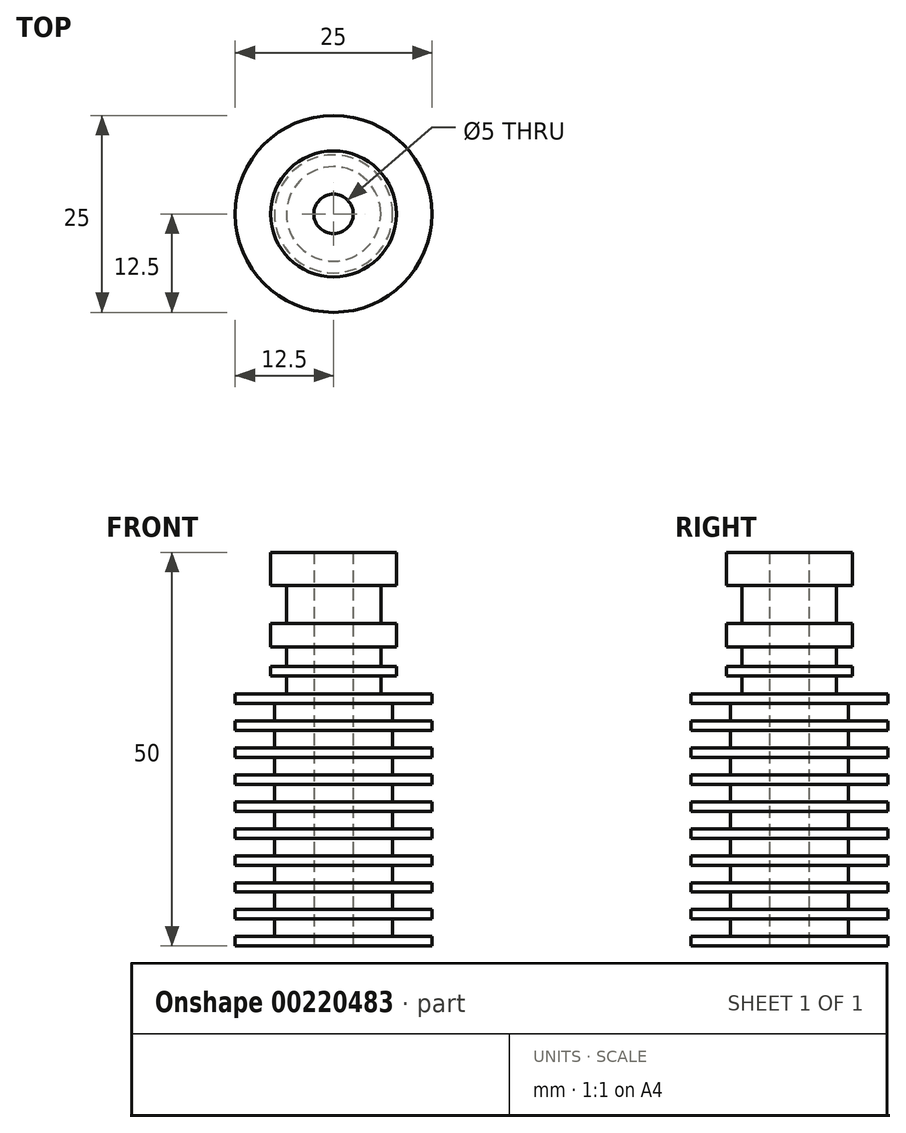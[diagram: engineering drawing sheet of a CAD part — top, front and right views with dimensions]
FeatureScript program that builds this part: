
annotation { "Feature Type Name" : "Feature", "Feature Type Description" : "" }
export const myFeature = defineFeature(function(context is Context, id is Id, definition is map)
    precondition{}
    {
        {
            var Q0;
            Q0=qCreatedBy(makeId("Front.planeOp"),FACE);
            var sketch = newSketch(context, id + "F0", { "sketchPlane" : qUnion([Q0])});
            skLineSegment(sketch, "E0", {"start": v(0, 0) * mm, "end": v(12.5, 0) * mm});
            skLineSegment(sketch, "E1", {"start": v(12.5, 0) * mm, "end": v(12.5, 1.2) * mm});
            skLineSegment(sketch, "E2", {"start": v(12.5, 1.2) * mm, "end": v(7.5, 1.2) * mm});
            skLineSegment(sketch, "E3", {"start": v(7.5, 1.2) * mm, "end": v(7.5, 3.42) * mm});
            skLineSegment(sketch, "E4", {"start": v(7.5, 3.42) * mm, "end": v(12.5, 3.42) * mm});
            skLineSegment(sketch, "E5", {"start": v(12.5, 3.42) * mm, "end": v(12.5, 4.62) * mm});
            skLineSegment(sketch, "E6", {"start": v(12.5, 4.62) * mm, "end": v(7.5, 4.62) * mm});
            skLineSegment(sketch, "E7", {"start": v(7.5, 4.62) * mm, "end": v(7.5, 6.84) * mm});
            skLineSegment(sketch, "E8", {"start": v(7.5, 6.84) * mm, "end": v(12.5, 6.84) * mm});
            skLineSegment(sketch, "E9", {"start": v(12.5, 6.84) * mm, "end": v(12.5, 8.04) * mm});
            skLineSegment(sketch, "E10", {"start": v(12.5, 8.04) * mm, "end": v(7.5, 8.04) * mm});
            skLineSegment(sketch, "E11", {"start": v(7.5, 8.04) * mm, "end": v(7.5, 10.27) * mm});
            skLineSegment(sketch, "E12", {"start": v(7.5, 10.27) * mm, "end": v(12.5, 10.27) * mm});
            skLineSegment(sketch, "E13", {"start": v(12.5, 10.27) * mm, "end": v(12.5, 11.47) * mm});
            skLineSegment(sketch, "E14", {"start": v(12.5, 11.47) * mm, "end": v(7.5, 11.47) * mm});
            skLineSegment(sketch, "E15", {"start": v(7.5, 11.47) * mm, "end": v(7.5, 13.69) * mm});
            skLineSegment(sketch, "E16", {"start": v(7.5, 13.69) * mm, "end": v(12.5, 13.69) * mm});
            skLineSegment(sketch, "E17", {"start": v(12.5, 13.69) * mm, "end": v(12.5, 14.89) * mm});
            skLineSegment(sketch, "E18", {"start": v(12.5, 14.89) * mm, "end": v(7.5, 14.89) * mm});
            skLineSegment(sketch, "E19", {"start": v(7.5, 14.89) * mm, "end": v(7.5, 17.11) * mm});
            skLineSegment(sketch, "E20", {"start": v(7.5, 17.11) * mm, "end": v(12.5, 17.11) * mm});
            skLineSegment(sketch, "E21", {"start": v(12.5, 17.11) * mm, "end": v(12.5, 18.31) * mm});
            skLineSegment(sketch, "E22", {"start": v(12.5, 18.31) * mm, "end": v(7.5, 18.31) * mm});
            skLineSegment(sketch, "E23", {"start": v(7.5, 18.31) * mm, "end": v(7.5, 20.53) * mm});
            skLineSegment(sketch, "E24", {"start": v(7.5, 20.53) * mm, "end": v(12.5, 20.53) * mm});
            skLineSegment(sketch, "E25", {"start": v(12.5, 20.53) * mm, "end": v(12.5, 21.73) * mm});
            skLineSegment(sketch, "E26", {"start": v(12.5, 21.73) * mm, "end": v(7.5, 21.73) * mm});
            skLineSegment(sketch, "E27", {"start": v(7.5, 21.73) * mm, "end": v(7.5, 23.96) * mm});
            skLineSegment(sketch, "E28", {"start": v(7.5, 23.96) * mm, "end": v(12.5, 23.96) * mm});
            skLineSegment(sketch, "E29", {"start": v(12.5, 23.96) * mm, "end": v(12.5, 25.16) * mm});
            skLineSegment(sketch, "E30", {"start": v(12.5, 25.16) * mm, "end": v(7.5, 25.16) * mm});
            skLineSegment(sketch, "E31", {"start": v(7.5, 25.16) * mm, "end": v(7.5, 27.38) * mm});
            skLineSegment(sketch, "E32", {"start": v(7.5, 27.38) * mm, "end": v(12.5, 27.38) * mm});
            skLineSegment(sketch, "E33", {"start": v(12.5, 27.38) * mm, "end": v(12.5, 28.58) * mm});
            skLineSegment(sketch, "E34", {"start": v(12.5, 28.58) * mm, "end": v(7.5, 28.58) * mm});
            skLineSegment(sketch, "E35", {"start": v(7.5, 28.58) * mm, "end": v(7.5, 30.8) * mm});
            skLineSegment(sketch, "E36", {"start": v(7.5, 30.8) * mm, "end": v(12.5, 30.8) * mm});
            skLineSegment(sketch, "E37", {"start": v(12.5, 30.8) * mm, "end": v(12.5, 32) * mm});
            skLineSegment(sketch, "E38", {"start": v(12.5, 32) * mm, "end": v(6, 32) * mm});
            skLineSegment(sketch, "E39", {"start": v(6, 32) * mm, "end": v(6, 34.3) * mm});
            skLineSegment(sketch, "E40", {"start": v(6, 34.3) * mm, "end": v(8, 34.3) * mm});
            skLineSegment(sketch, "E41", {"start": v(8, 34.3) * mm, "end": v(8, 35.5) * mm});
            skLineSegment(sketch, "E42", {"start": v(8, 35.5) * mm, "end": v(6, 35.5) * mm});
            skLineSegment(sketch, "E43", {"start": v(6, 35.5) * mm, "end": v(6, 38) * mm});
            skLineSegment(sketch, "E44", {"start": v(6, 38) * mm, "end": v(8, 38) * mm});
            skLineSegment(sketch, "E45", {"start": v(8, 38) * mm, "end": v(8, 41) * mm});
            skLineSegment(sketch, "E46", {"start": v(8, 41) * mm, "end": v(6, 41) * mm});
            skLineSegment(sketch, "E47", {"start": v(6, 41) * mm, "end": v(6, 45.8) * mm});
            skLineSegment(sketch, "E48", {"start": v(6, 45.8) * mm, "end": v(8, 45.8) * mm});
            skLineSegment(sketch, "E49", {"start": v(8, 45.8) * mm, "end": v(8, 50) * mm});
            skLineSegment(sketch, "E50", {"start": v(8, 50) * mm, "end": v(0, 50) * mm});
            skLineSegment(sketch, "E51", {"start": v(0, 50) * mm, "end": v(0, 0) * mm});
            skSolve(sketch);
        }
        {
            var Q0;
            Q0 = qSketchRegion(id + "F0", true);
            var Q1;
            Q1=sQuery(id+"F0.wireOp",EDGE,"E51");
            revolve(context, id + "F1", {"entities" : qUnion([Q0]), "axis" : qUnion([Q1]), "revolveType" : RevolveType.FULL});
        }
        {
            var Q0;
            Q0=makeQuery(id+"F1.opRevolve","SWEPT_FACE",FACE,{"disambiguationData":[OSD([sQuery(id+"F0.wireOp",EDGE,"E0")])]});
            var sketch = newSketch(context, id + "F2", { "sketchPlane" : qUnion([Q0])});
            skCircle(sketch, "E52", {"center": v(0, 0) * mm, "radius": 2.5 * mm});
            skSolve(sketch);
        }
        {
            var Q0;
            Q0 = qSketchRegion(id + "F2", true);
            extrude(context, id + "F3", {"entities" : qUnion([Q0]), "operationType" : NewBodyOperationType.REMOVE, "endBound" : BoundingType.THROUGH_ALL, "oppositeDirection" : true, "depth" : 25 * mm});
        }
    });
